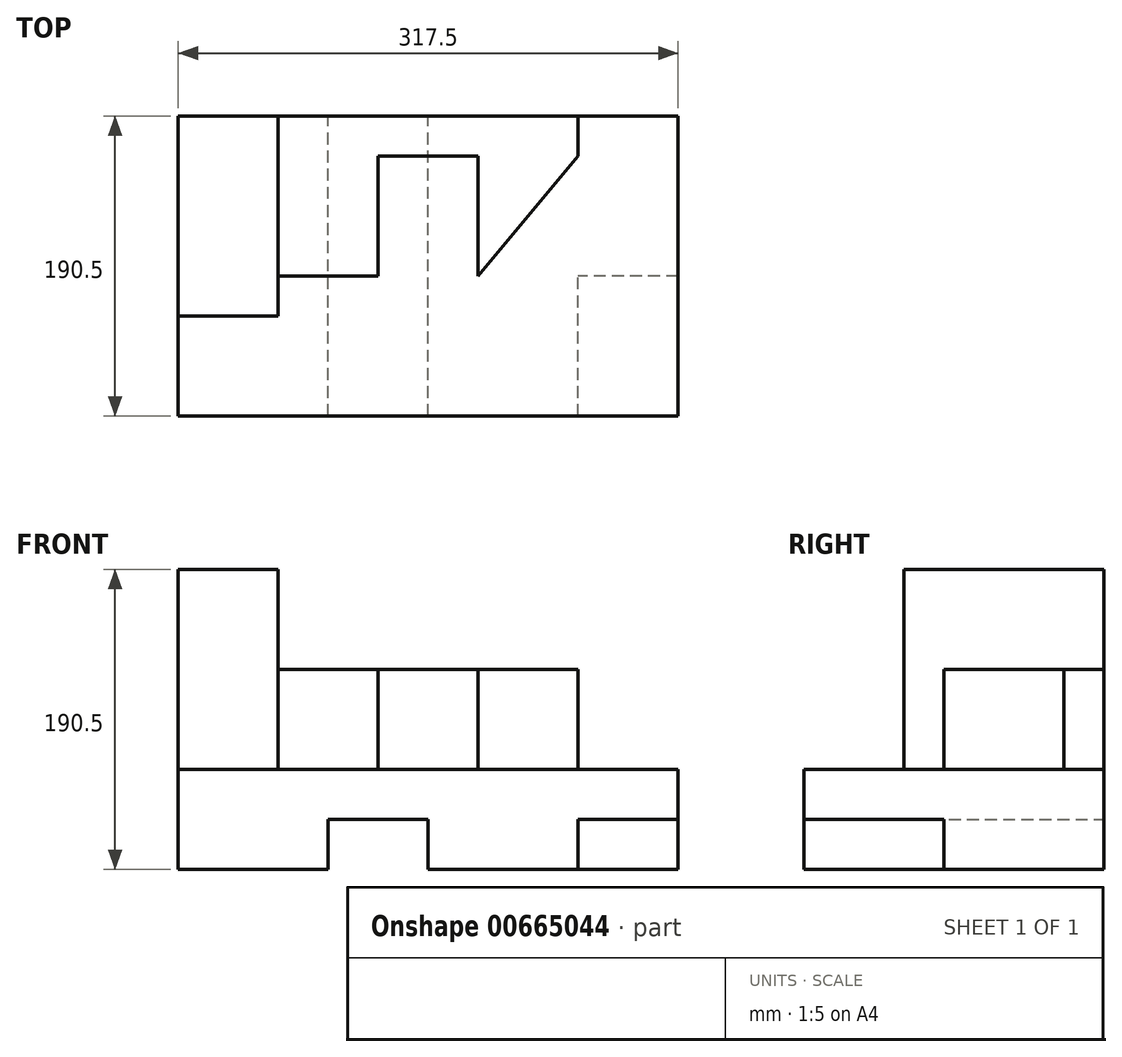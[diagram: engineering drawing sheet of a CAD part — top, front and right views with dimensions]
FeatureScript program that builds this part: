
annotation { "Feature Type Name" : "Feature", "Feature Type Description" : "" }
export const myFeature = defineFeature(function(context is Context, id is Id, definition is map)
    precondition{}
    {
        {
            var Q0;
            Q0=qCreatedBy(makeId("Front.planeOp"),FACE);
            var sketch = newSketch(context, id + "F0", { "sketchPlane" : qUnion([Q0])});
            skLineSegment(sketch, "E0", {"start": v(0, 0) * mm, "end": v(0, 63.5) * mm});
            skLineSegment(sketch, "E1", {"start": v(0, 63.5) * mm, "end": v(317.5, 63.5) * mm});
            skLineSegment(sketch, "E2", {"start": v(317.5, 63.5) * mm, "end": v(317.5, 31.75) * mm});
            skLineSegment(sketch, "E3", {"start": v(317.5, 31.75) * mm, "end": v(254, 31.75) * mm});
            skLineSegment(sketch, "E4", {"start": v(254, 31.75) * mm, "end": v(254, 0) * mm});
            skLineSegment(sketch, "E5", {"start": v(254, 0) * mm, "end": v(158.75, 0) * mm});
            skLineSegment(sketch, "E6", {"start": v(158.75, 0) * mm, "end": v(158.75, 31.75) * mm});
            skLineSegment(sketch, "E7", {"start": v(158.75, 31.75) * mm, "end": v(95.25, 31.75) * mm});
            skLineSegment(sketch, "E8", {"start": v(95.25, 31.75) * mm, "end": v(95.25, 0) * mm});
            skLineSegment(sketch, "E9", {"start": v(95.25, 0) * mm, "end": v(0, 0) * mm});
            skSolve(sketch);
        }
        {
            var Q0;
            Q0 = qSketchRegion(id + "F0", true);
            extrude(context, id + "F1", {"entities" : qUnion([Q0]), "endBound" : BoundingType.SYMMETRIC, "depth" : 190.5 * mm, "offsetDistance" : 25.4 * mm});
        }
        {
            var Q0;
            Q0=makeQuery(id+"F1.opExtrude","CAP_FACE",FACE,{"disambiguationData":[OSD([sQuery(id+"F0.wireOp",EDGE,"E0"),sQuery(id+"F0.wireOp",EDGE,"E1"),sQuery(id+"F0.wireOp",EDGE,"E2"),sQuery(id+"F0.wireOp",EDGE,"E3"),sQuery(id+"F0.wireOp",EDGE,"E4"),sQuery(id+"F0.wireOp",EDGE,"E5"),sQuery(id+"F0.wireOp",EDGE,"E6"),sQuery(id+"F0.wireOp",EDGE,"E7"),sQuery(id+"F0.wireOp",EDGE,"E8"),sQuery(id+"F0.wireOp",EDGE,"E9")])],"isStart":true});
            var sketch = newSketch(context, id + "F2", { "sketchPlane" : qUnion([Q0])});
            skLineSegment(sketch, "E10.bottom", {"start": v(-317.5, 31.75) * mm, "end": v(-254, 31.75) * mm});
            skLineSegment(sketch, "E10.top", {"start": v(-317.5, 0) * mm, "end": v(-254, 0) * mm});
            skLineSegment(sketch, "E10.left", {"start": v(-317.5, 31.75) * mm, "end": v(-317.5, 0) * mm});
            skLineSegment(sketch, "E10.right", {"start": v(-254, 31.75) * mm, "end": v(-254, 0) * mm});
            skSolve(sketch);
        }
        {
            var Q0;
            Q0=makeQuery(id+"F2.imprint","IMPRINT",FACE,{"disambiguationData":[TD([[makeQuery(id+"F2.imprint","IMPRINT",EDGE,{"derivedFrom":sQuery(id+"F2.wireOp",EDGE,"E10.bottom")}),-1.0]])]});
            extrude(context, id + "F3", {"entities" : qUnion([Q0]), "operationType" : NewBodyOperationType.ADD, "oppositeDirection" : true, "depth" : 101.6 * mm, "offsetDistance" : 25.4 * mm});
        }
        {
            var Q0;
            Q0=makeQuery(id+"F1.opExtrude","CAP_FACE",FACE,{"disambiguationData":[OSD([sQuery(id+"F0.wireOp",EDGE,"E0"),sQuery(id+"F0.wireOp",EDGE,"E1"),sQuery(id+"F0.wireOp",EDGE,"E2"),sQuery(id+"F0.wireOp",EDGE,"E3"),sQuery(id+"F0.wireOp",EDGE,"E4"),sQuery(id+"F0.wireOp",EDGE,"E5"),sQuery(id+"F0.wireOp",EDGE,"E6"),sQuery(id+"F0.wireOp",EDGE,"E7"),sQuery(id+"F0.wireOp",EDGE,"E8"),sQuery(id+"F0.wireOp",EDGE,"E9")])],"isStart":false});
            var sketch = newSketch(context, id + "F4", { "sketchPlane" : qUnion([Q0])});
            skLineSegment(sketch, "E11.bottom", {"start": v(0, 63.5) * mm, "end": v(63.5, 63.5) * mm});
            skLineSegment(sketch, "E11.top", {"start": v(0, 190.5) * mm, "end": v(63.5, 190.5) * mm});
            skLineSegment(sketch, "E11.left", {"start": v(0, 63.5) * mm, "end": v(0, 190.5) * mm});
            skLineSegment(sketch, "E11.right", {"start": v(63.5, 63.5) * mm, "end": v(63.5, 190.5) * mm});
            skSolve(sketch);
        }
        {
            var Q0;
            Q0 = qSketchRegion(id + "F4", true);
            extrude(context, id + "F5", {"entities" : qUnion([Q0]), "operationType" : NewBodyOperationType.ADD, "oppositeDirection" : true, "depth" : 190.5 * mm, "offsetDistance" : 25.4 * mm, "hasSecondDirection" : true, "secondDirectionOppositeDirection" : true, "secondDirectionDepth" : 63.5 * mm});
        }
        {
            var Q0;
            Q0=makeQuery(id+"F5.opExtrude","SWEPT_FACE",FACE,{"disambiguationData":[OSD([sQuery(id+"F4.wireOp",EDGE,"E11.top")])]});
            var sketch = newSketch(context, id + "F6", { "sketchPlane" : qUnion([Q0])});
            skLineSegment(sketch, "E12", {"start": v(63.5, 95.25) * mm, "end": v(254, 95.25) * mm});
            skLineSegment(sketch, "E13", {"start": v(254, 95.25) * mm, "end": v(254, 69.85) * mm});
            skLineSegment(sketch, "E14", {"start": v(127, 69.85) * mm, "end": v(127, -6.35) * mm});
            skLineSegment(sketch, "E15", {"start": v(127, -6.35) * mm, "end": v(63.5, -6.35) * mm});
            skLineSegment(sketch, "E16", {"start": v(63.5, -6.35) * mm, "end": v(63.5, 95.25) * mm});
            skLineSegment(sketch, "E17", {"start": v(190.5, -6.35) * mm, "end": v(254, 69.85) * mm});
            skLineSegment(sketch, "E18", {"start": v(190.5, -6.35) * mm, "end": v(190.5, 69.85) * mm});
            skLineSegment(sketch, "E19", {"start": v(127, 69.85) * mm, "end": v(190.5, 69.85) * mm});
            skSolve(sketch);
        }
        {
            var Q0;
            Q0=makeQuery(id+"F6.imprint","IMPRINT",FACE,{"disambiguationData":[TD([[makeQuery(id+"F6.imprint","IMPRINT",EDGE,{"derivedFrom":sQuery(id+"F6.wireOp",EDGE,"E12")}),-1.0]])]});
            extrude(context, id + "F7", {"entities" : qUnion([Q0]), "operationType" : NewBodyOperationType.ADD, "oppositeDirection" : true, "depth" : 139.7 * mm, "offsetDistance" : 25.4 * mm, "hasSecondDirection" : true, "secondDirectionOppositeDirection" : true, "secondDirectionDepth" : 63.5 * mm});
        }
    });
